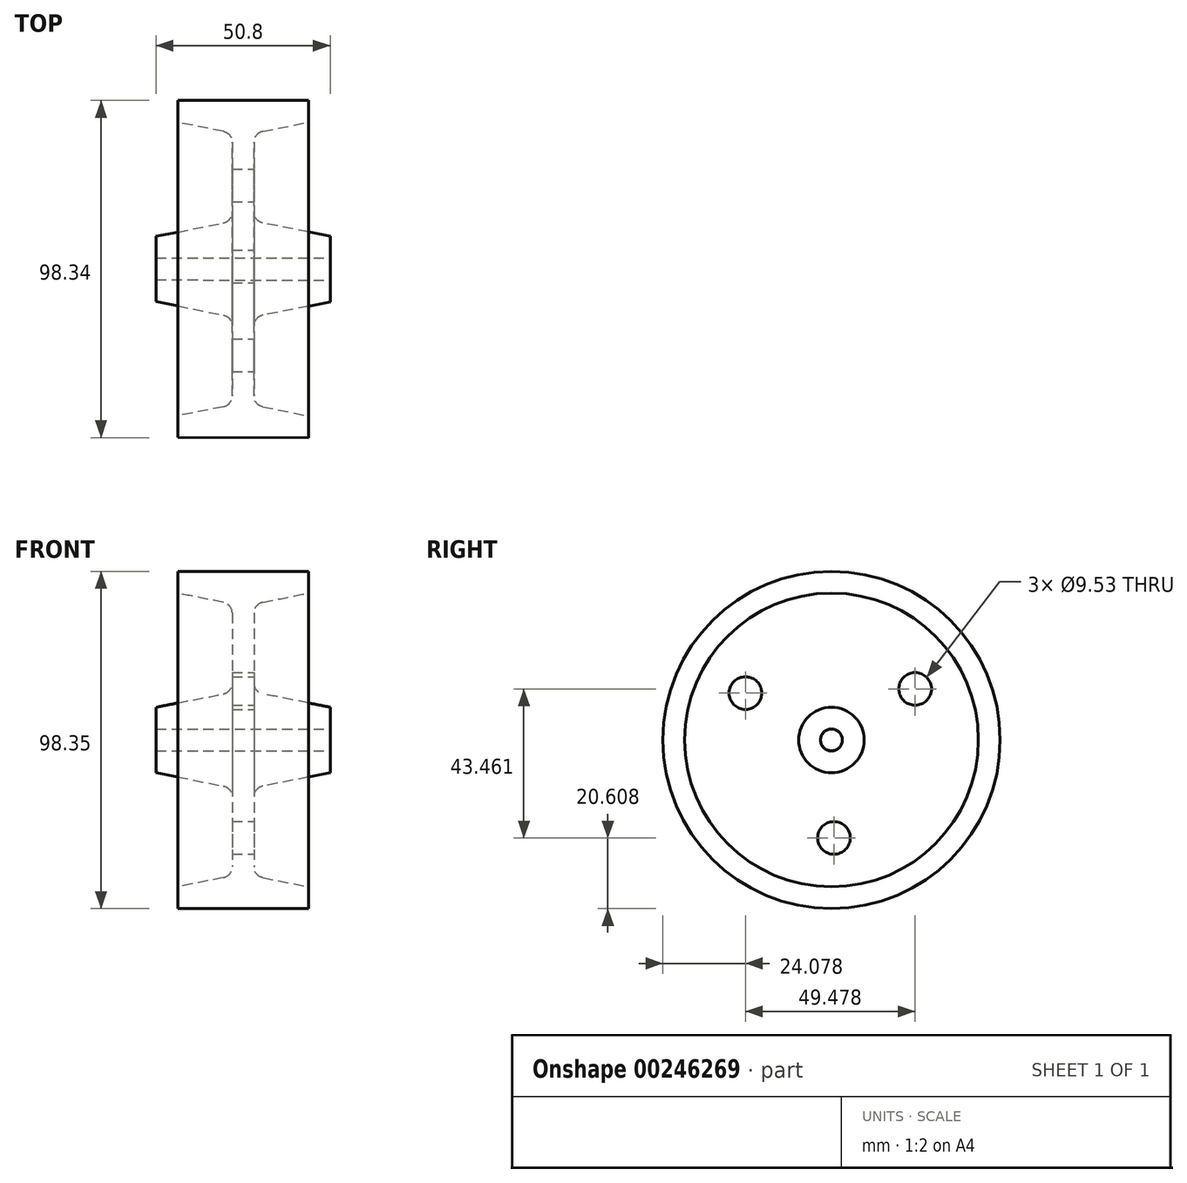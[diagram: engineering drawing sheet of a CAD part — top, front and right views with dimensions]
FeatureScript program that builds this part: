
annotation { "Feature Type Name" : "Feature", "Feature Type Description" : "" }
export const myFeature = defineFeature(function(context is Context, id is Id, definition is map)
    precondition{}
    {
        {
            var Q0;
            Q0=qCreatedBy(makeId("Front.planeOp"),FACE);
            var sketch = newSketch(context, id + "F0", { "sketchPlane" : qUnion([Q0])});
            skLineSegment(sketch, "E0", {"start": v(25.4, -2.34) * mm, "end": v(25.4, 4.01) * mm});
            skLineSegment(sketch, "E1", {"start": v(5.73, 7.92) * mm, "end": v(25.4, 4.01) * mm});
            skLineSegment(sketch, "E2", {"start": v(3.17, 11.04) * mm, "end": v(3.17, 31.5) * mm});
            skLineSegment(sketch, "E3", {"start": v(19.05, 43.64) * mm, "end": v(19.05, 37.29) * mm});
            skLineSegment(sketch, "E4", {"start": v(19.05, 37.29) * mm, "end": v(5.73, 34.62) * mm});
            skPoint(sketch, "E5.visualSharp", {"position": v(3.17, 34.11) * mm});
            skArc(sketch, "E5.filletArc", {"start": v(5.73, 34.62) * mm, "mid": v(3.9, 33.52) * mm, "end": v(3.17, 31.5) * mm});
            skPoint(sketch, "E6.visualSharp", {"position": v(3.17, 8.43) * mm});
            skArc(sketch, "E6.filletArc", {"start": v(3.17, 11.04) * mm, "mid": v(3.9, 9.02) * mm, "end": v(5.73, 7.92) * mm});
            skArc(sketch, "E7.MirrorCS", {"start": v(-3.17, 11.01) * mm, "mid": v(-3.9, 9) * mm, "end": v(-5.73, 7.9) * mm});
            skArc(sketch, "E8.MirrorCS", {"start": v(-5.73, 34.6) * mm, "mid": v(-3.9, 33.5) * mm, "end": v(-3.17, 31.49) * mm});
            skLineSegment(sketch, "E9.MirrorCS", {"start": v(-25.4, -2.36) * mm, "end": v(-25.4, 3.99) * mm});
            skPoint(sketch, "E10.MirrorP", {"position": v(-3.17, 34.11) * mm});
            skLineSegment(sketch, "E11.MirrorCS", {"start": v(-5.73, 7.9) * mm, "end": v(-25.4, 3.99) * mm});
            skLineSegment(sketch, "E12.MirrorCS", {"start": v(-3.17, 11.01) * mm, "end": v(-3.17, 31.49) * mm});
            skPoint(sketch, "E13.MirrorP", {"position": v(-3.17, 8.43) * mm});
            skLineSegment(sketch, "E14.MirrorCS", {"start": v(-19.05, 43.61) * mm, "end": v(-19.05, 37.26) * mm});
            skLineSegment(sketch, "E15.MirrorCS", {"start": v(-19.05, 37.26) * mm, "end": v(-5.73, 34.6) * mm});
            skLineSegment(sketch, "E16", {"start": v(-25.4, -5.54) * mm, "end": v(26.14, -5.54) * mm});
            skLineSegment(sketch, "E17", {"start": v(-19.05, 43.61) * mm, "end": v(19.05, 43.64) * mm});
            skLineSegment(sketch, "E18", {"start": v(25.4, -2.34) * mm, "end": v(-25.4, -2.36) * mm});
            skSolve(sketch);
        }
        {
            var Q0;
            Q0=makeQuery(id+"F0.imprint","IMPRINT",FACE,{"disambiguationData":[TD([[makeQuery(id+"F0.imprint","IMPRINT",EDGE,{"derivedFrom":sQuery(id+"F0.wireOp",EDGE,"E0")}),1.0]])]});
            var Q1;
            Q1=sQuery(id+"F0.wireOp",EDGE,"E16");
            revolve(context, id + "F1", {"entities" : qUnion([Q0]), "axis" : qUnion([Q1]), "revolveType" : RevolveType.FULL});
        }
        {
            var Q0;
            Q0=makeQuery(id+"F1.opRevolve","SWEPT_FACE",FACE,{"disambiguationData":[OSD([sQuery(id+"F0.wireOp",EDGE,"E0")])]});
            var sketch = newSketch(context, id + "F2", { "sketchPlane" : qUnion([Q0])});
            skCircle(sketch, "E19", {"center": v(24.39, 9.36) * mm, "radius": 4.76 * mm});
            skCircle(sketch, "E20", {"center": v(-25.1, 8.14) * mm, "radius": 4.76 * mm});
            skCircle(sketch, "E21", {"center": v(0.7, -34.1) * mm, "radius": 4.76 * mm});
            skSolve(sketch);
        }
        {
            var Q0;
            Q0=makeQuery(id+"F2.imprint","IMPRINT",FACE,{"disambiguationData":[TD([[makeQuery(id+"F2.imprint","IMPRINT",EDGE,{"derivedFrom":sQuery(id+"F2.wireOp",EDGE,"E20")}),1.0]])]});
            extrude(context, id + "F3", {"entities" : qUnion([Q0]), "operationType" : NewBodyOperationType.REMOVE, "endBound" : BoundingType.THROUGH_ALL, "oppositeDirection" : true, "depth" : 25.4 * mm});
        }
        {
            var Q0;
            Q0=makeQuery(id+"F2.imprint","IMPRINT",FACE,{"disambiguationData":[TD([[makeQuery(id+"F2.imprint","IMPRINT",EDGE,{"derivedFrom":sQuery(id+"F2.wireOp",EDGE,"E21")}),1.0]])]});
            extrude(context, id + "F4", {"entities" : qUnion([Q0]), "operationType" : NewBodyOperationType.REMOVE, "endBound" : BoundingType.THROUGH_ALL, "oppositeDirection" : true, "depth" : 25.4 * mm});
        }
        {
            var Q0;
            Q0=makeQuery(id+"F2.imprint","IMPRINT",FACE,{"disambiguationData":[TD([[makeQuery(id+"F2.imprint","IMPRINT",EDGE,{"derivedFrom":sQuery(id+"F2.wireOp",EDGE,"E19")}),1.0]])]});
            extrude(context, id + "F5", {"entities" : qUnion([Q0]), "operationType" : NewBodyOperationType.REMOVE, "endBound" : BoundingType.THROUGH_ALL, "oppositeDirection" : true, "depth" : 25.4 * mm});
        }
    });
